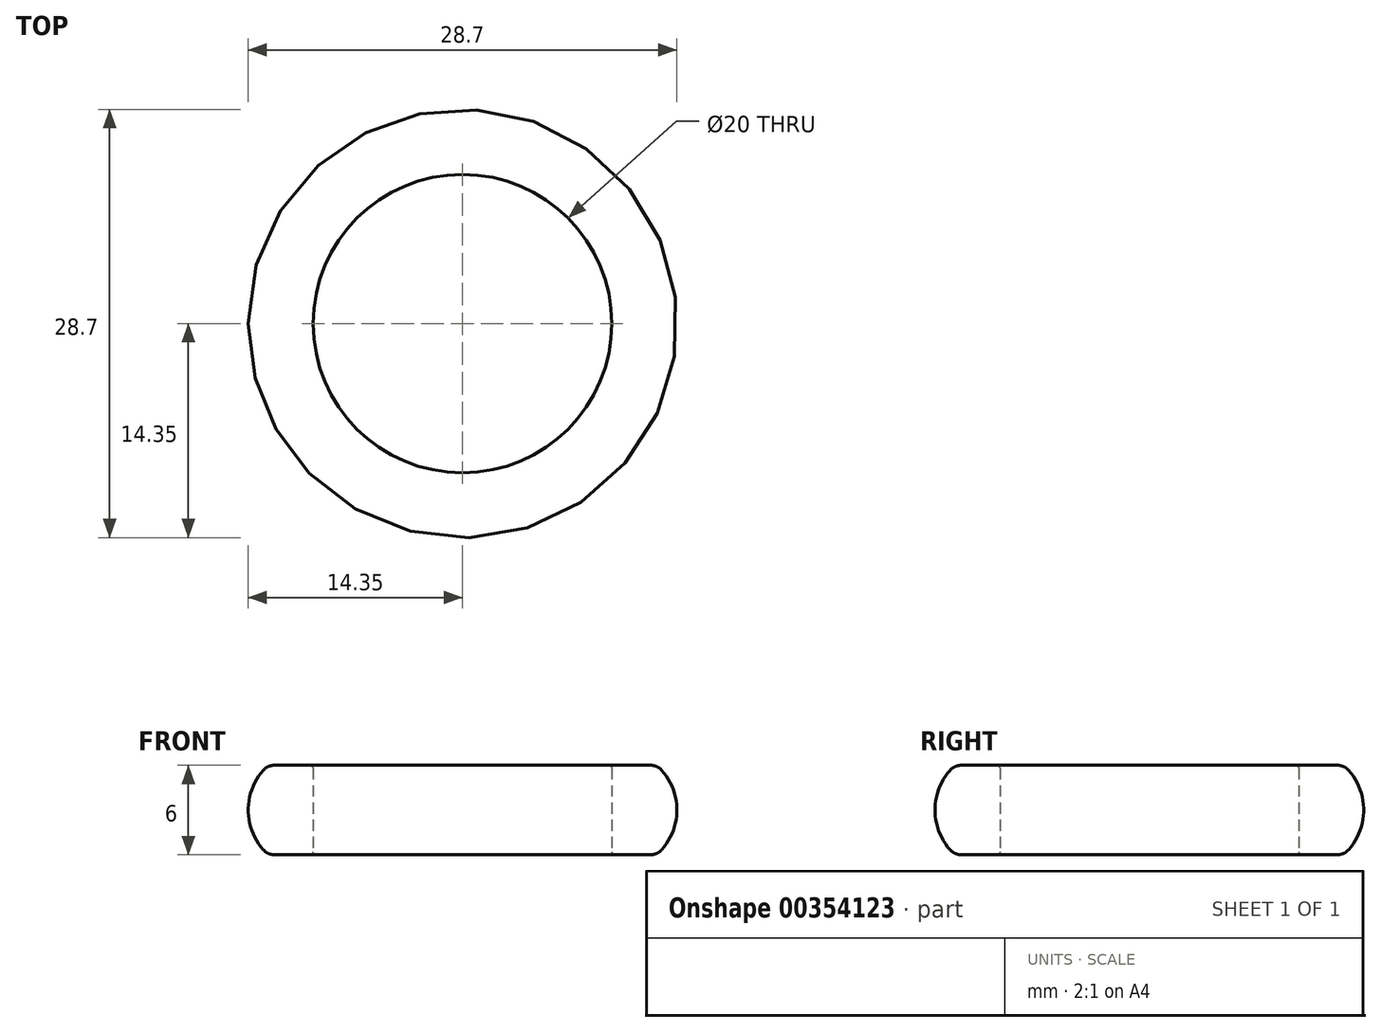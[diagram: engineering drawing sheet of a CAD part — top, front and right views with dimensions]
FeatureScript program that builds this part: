
annotation { "Feature Type Name" : "Feature", "Feature Type Description" : "" }
export const myFeature = defineFeature(function(context is Context, id is Id, definition is map)
    precondition{}
    {
        {
            var Q0;
            Q0=qCreatedBy(makeId("Front.planeOp"),FACE);
            var sketch = newSketch(context, id + "F0", { "sketchPlane" : qUnion([Q0])});
            skLineSegment(sketch, "E0", {"start": v(0, 0.2) * mm, "end": v(0, 5.8) * mm});
            skLineSegment(sketch, "E1", {"start": v(-0.2, 0) * mm, "end": v(-2.6, 0) * mm});
            skLineSegment(sketch, "E2", {"start": v(-0.2, 6) * mm, "end": v(-2.6, 6) * mm});
            skArc(sketch, "E3", {"start": v(-3.34, 5.67) * mm, "mid": v(-4.35, 3) * mm, "end": v(-3.34, 0.33) * mm});
            skPoint(sketch, "E4.visualSharp", {"position": v(-3, 6) * mm});
            skArc(sketch, "E4.filletArc", {"start": v(-2.6, 6) * mm, "mid": v(-3, 5.91) * mm, "end": v(-3.34, 5.67) * mm});
            skPoint(sketch, "E5.visualSharp", {"position": v(-3, 0) * mm});
            skArc(sketch, "E5.filletArc", {"start": v(-3.34, 0.33) * mm, "mid": v(-3, 0.09) * mm, "end": v(-2.6, 0) * mm});
            skPoint(sketch, "E6.visualSharp", {"position": v(0, 0) * mm});
            skArc(sketch, "E6.filletArc", {"start": v(-0.2, 0) * mm, "mid": v(-0.06, 0.06) * mm, "end": v(0, 0.2) * mm});
            skPoint(sketch, "E7.visualSharp", {"position": v(0, 6) * mm});
            skArc(sketch, "E7.filletArc", {"start": v(0, 5.8) * mm, "mid": v(-0.06, 5.94) * mm, "end": v(-0.2, 6) * mm});
            skLineSegment(sketch, "E8.0", {"start": v(10, 0.2) * mm, "end": v(10, 5.8) * mm});
            skSolve(sketch);
        }
        {
            var Q0;
            Q0=makeQuery(id+"F0.imprint","IMPRINT",FACE,{"disambiguationData":[TD([[makeQuery(id+"F0.imprint","IMPRINT",EDGE,{"derivedFrom":sQuery(id+"F0.wireOp",EDGE,"E0")}),1.0]])]});
            var Q1;
            Q1=sQuery(id+"F0.wireOp",EDGE,"E8.0");
            revolve(context, id + "F1", {"entities" : qUnion([Q0]), "axis" : qUnion([Q1]), "revolveType" : RevolveType.FULL});
        }
    });
